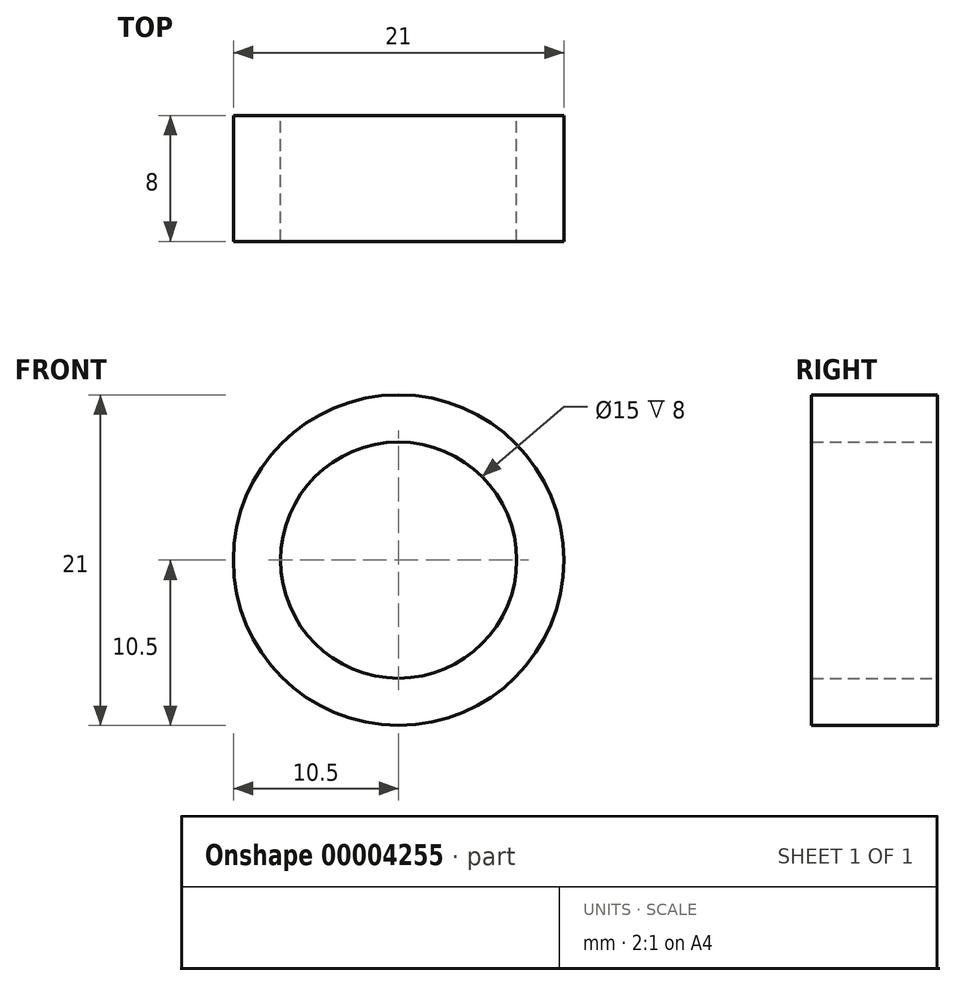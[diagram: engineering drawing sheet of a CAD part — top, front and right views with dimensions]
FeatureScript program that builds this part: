
annotation { "Feature Type Name" : "Feature", "Feature Type Description" : "" }
export const myFeature = defineFeature(function(context is Context, id is Id, definition is map)
    precondition{}
    {
        {
            var Q0;
            Q0=qCreatedBy(makeId("Front.planeOp"),FACE);
            var sketch = newSketch(context, id + "F0", { "sketchPlane" : qUnion([Q0])});
            skCircle(sketch, "E0", {"center": v(0, 0) * mm, "radius": 7.5 * mm});
            skCircle(sketch, "E1", {"center": v(0, 0) * mm, "radius": 10.5 * mm});
            skSolve(sketch);
        }
        {
            var Q0;
            Q0 = qSketchRegion(id + "F0", true);
            extrude(context, id + "F1", {"entities" : qUnion([Q0]), "depth" : 8 * mm, "symmetric" : true});
        }
    });
